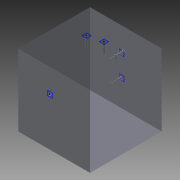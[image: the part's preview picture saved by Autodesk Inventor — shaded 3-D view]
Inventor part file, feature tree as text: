
AUTODESK INVENTOR PART (.ipt)
format: ipt  version: 2014 (Build 180170000, 170)  size: 423,424 bytes
history: native  units: mm
features: other x55, sketch x8, extrude x1
ambient origin geometry x8: Origin, YZ Plane, XZ Plane, XY Plane, X Axis, Y Axis, Z Axis, Center Point
bodies: 实体1 (feature_tree)
feature tree (64):
  extrude  "拉伸1"  TaperAngle=0.0deg  [1 undecoded]
  other  "UCS1"
  other  "UCS2"
  other  "UCS3"
  other  "UCS4"
  other  "UCS5"
  other  "UCS6"
  other  "Footprint1"
  other  "Footprint2"
  other  "Footprint3"
  other  "Footprint4"
  other  "Footprint5"
  other  "删除面1"
  other  "删除面2"
  sketch  "草图1"  dims[d0=1000.0mm d1=0.0mm]
  other  "UCS1: YZ 平面"
  other  "UCS1: XZ 平面"
  other  "UCS1: XY 平面"
  other  "UCS1: X 轴"
  other  "UCS1: Y 轴"
  other  "UCS1: Z 轴"
  other  "UCS1: 原点"
  other  "UCS2: YZ 平面"
  other  "UCS2: XZ 平面"
  other  "UCS2: XY 平面"
  other  "UCS2: X 轴"
  other  "UCS2: Y 轴"
  other  "UCS2: Z 轴"
  other  "UCS2: 原点"
  other  "UCS3: YZ 平面"
  other  "UCS3: XZ 平面"
  other  "UCS3: XY 平面"
  other  "UCS3: X 轴"
  other  "UCS3: Y 轴"
  other  "UCS3: Z 轴"
  other  "UCS3: 原点"
  other  "UCS4: YZ 平面"
  other  "UCS4: XZ 平面"
  other  "UCS4: XY 平面"
  other  "UCS4: X 轴"
  other  "UCS4: Y 轴"
  other  "UCS4: Z 轴"
  other  "UCS4: 原点"
  other  "UCS5: YZ 平面"
  other  "UCS5: XZ 平面"
  other  "UCS5: XY 平面"
  other  "UCS5: X 轴"
  other  "UCS5: Y 轴"
  other  "UCS5: Z 轴"
  other  "UCS5: 原点"
  other  "UCS6: YZ 平面"
  other  "UCS6: XZ 平面"
  other  "UCS6: XY 平面"
  other  "UCS6: X 轴"
  other  "UCS6: Y 轴"
  other  "UCS6: Z 轴"
  other  "UCS6: 原点"
  sketch  "草图2"  dims[d2=0.0mm d3=0.0mm d4=0.0mm d5=0.0mm d6=0.0mm d7=0.0mm]
  sketch  "草图3"  dims[d8=0.0mm d9=0.0mm d10=0.0mm d11=0.0mm d12=0.0mm d13=0.0mm]
  sketch  "草图8"  dims[d14=0.0mm d15=0.0mm d16=0.0mm d17=0.0mm d18=0.0mm d19=0.0mm]
  sketch  "草图10"  dims[d20=0.0mm d21=0.0mm d22=0.0mm d23=0.0mm d24=0.0mm d25=0.0mm]
  sketch  "草图12"  dims[d26=0.0mm d27=0.0mm d28=0.0mm d29=0.0mm d30=0.0mm d31=0.0mm]
  sketch  "草图14"  dims[d32=0.0mm d33=0.0mm d34=0.0mm d35=0.0mm d36=0.0mm d37=0.0mm d38=0.0mm]
  sketch  "草图16"  dims[d42=0.0mm d46=0.0mm d52=0.0mm d58=0.0mm d64=0.0mm d70=0.0mm d76=0.0mm d82=0.0mm]
note: 1 required parameter value undecoded (feature->parameter linkage not recoverable at this tier; creation-order binding heuristic only, values carry confidence <= 0.55)
